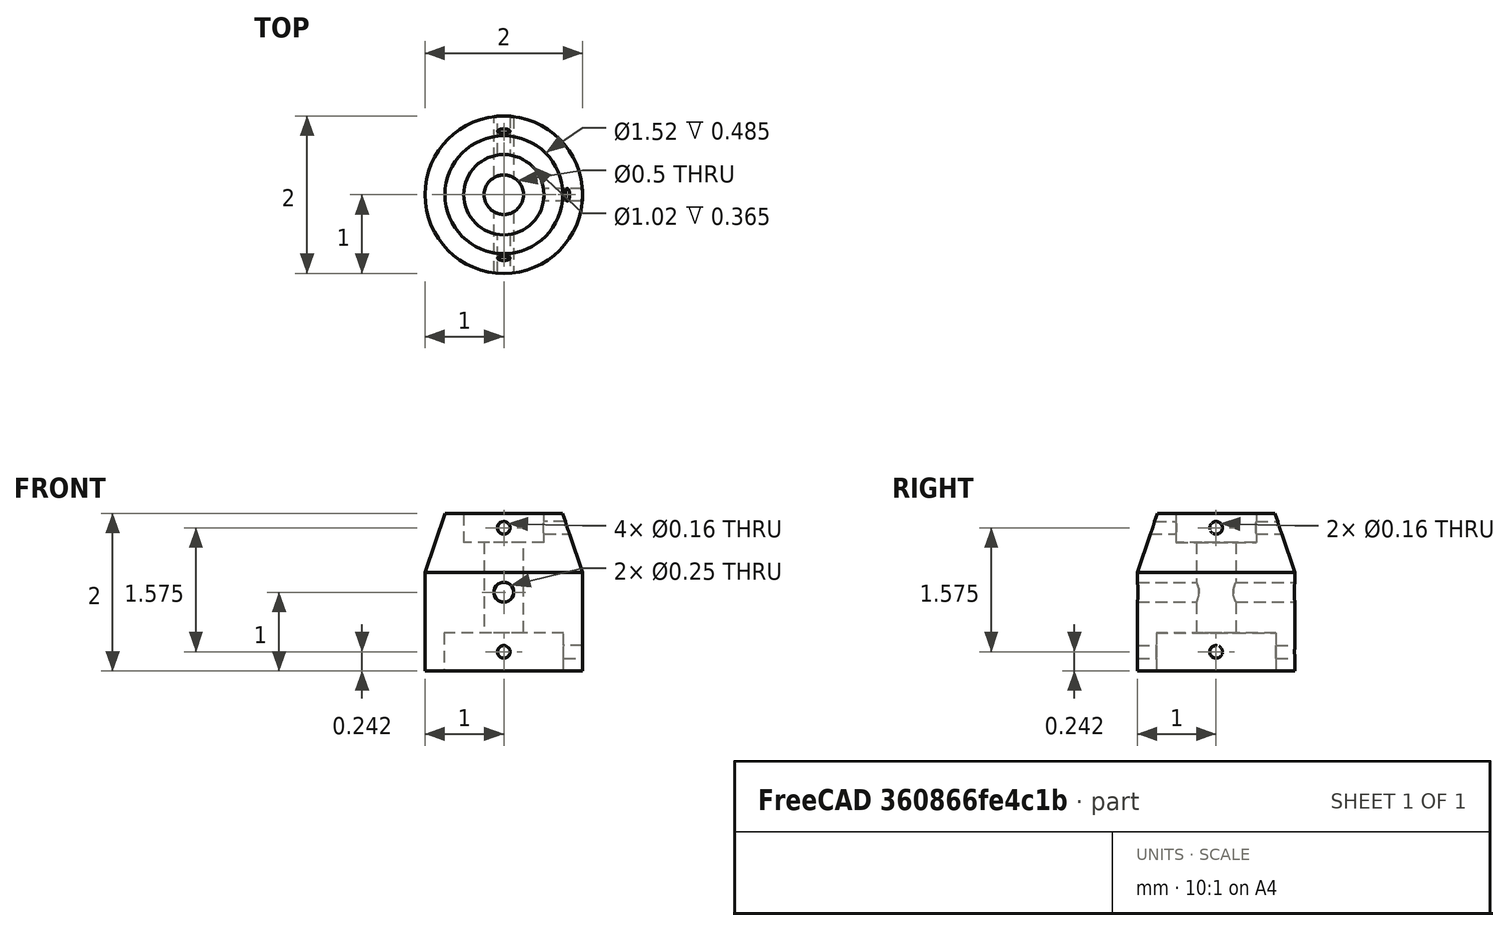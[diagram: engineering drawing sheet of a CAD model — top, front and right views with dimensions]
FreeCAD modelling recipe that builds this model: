
FCSTD DOCUMENT  (FreeCAD 0.20R29410 (Git))
Label: round_dies
License: All rights reserved
LicenseURL: http://en.wikipedia.org/wiki/All_rights_reserved
objects: Part::Cylinder×9, TechDraw::DrawViewDimension×9, TechDraw::DrawViewBalloon×7, TechDraw::DrawViewDimExtent×6, TechDraw::DrawProjGroupItem×2, TechDraw::DrawViewSection×2, Part::Cone×1, Part::Fuse×1, Part::MultiFuse×1, Part::Cut×1, TechDraw::DrawSVGTemplate×1, TechDraw::DrawProjGroup×1, TechDraw::DrawViewPart×1, TechDraw::DrawViewAnnotation×1, TechDraw::DrawPage×1
note: 13 computed .brp shape members not serialized (recipe doc carries the construction recipe); baked Part::Feature solids carry a one-line shape summary decoded from their .brp

FEATURE [Part::Cylinder] cylinder
  Angle = 360
  AttacherType = Attacher::AttachEngine3D
  FirstAngle = 0
  Height = 1.25
  Radius = 1
  SecondAngle = 0
FEATURE [Part::Cone] cylinder001
  Angle = 360
  AttacherType = Attacher::AttachEngine3D
  Height = 0.75
  Placement = pos=(0,0,1.25) rot=(0,0,1;0rad)
  Radius1 = 1
  Radius2 = 0.749
FEATURE [Part::Fuse] union
  Base = -> cylinder
  Tool = -> cylinder001
FEATURE [Part::Cylinder] cylinder002
  Angle = 360
  AttacherType = Attacher::AttachEngine3D
  FirstAngle = 0
  Height = 2.2
  Placement = pos=(0,0,-0.1) rot=(0,0,1;0rad)
  Radius = 0.2505
  SecondAngle = 0
FEATURE [Part::Cylinder] cylinder003
  Angle = 360
  AttacherType = Attacher::AttachEngine3D
  FirstAngle = 0
  Height = 0.585
  Placement = pos=(0,0,-0.1) rot=(0,0,1;0rad)
  Radius = 0.761
  SecondAngle = 0
FEATURE [Part::Cylinder] cylinder004
  Angle = 360
  AttacherType = Attacher::AttachEngine3D
  FirstAngle = 0
  Height = 0.465
  Placement = pos=(0,0,1.635) rot=(0,0,1;0rad)
  Radius = 0.51
  SecondAngle = 0
FEATURE [Part::Cylinder] cylinder005
  Angle = 360
  AttacherType = Attacher::AttachEngine3D
  FirstAngle = 0
  Height = 2.2
  Placement = pos=(0,1.1,1) rot=(1,0,0;1.5708rad)
  Radius = 0.1255
  SecondAngle = 0
FEATURE [Part::Cylinder] cylinder006
  Angle = 360
  AttacherType = Attacher::AttachEngine3D
  FirstAngle = 0
  Height = 2.2
  Placement = pos=(0,1.1,0.2425) rot=(1,0,0;1.5708rad)
  Radius = 0.0805
  SecondAngle = 0
FEATURE [Part::Cylinder] cylinder007
  Angle = 360
  AttacherType = Attacher::AttachEngine3D
  FirstAngle = 0
  Height = 2.2
  Placement = pos=(0,0,0.2425) rot=(0,1,0;1.5708rad)
  Radius = 0.0805
  SecondAngle = 0
FEATURE [Part::Cylinder] cylinder008
  Angle = 360
  AttacherType = Attacher::AttachEngine3D
  FirstAngle = 0
  Height = 2.2
  Placement = pos=(0,1.1,1.8175) rot=(1,0,0;1.5708rad)
  Radius = 0.0805
  SecondAngle = 0
FEATURE [Part::Cylinder] cylinder009
  Angle = 360
  AttacherType = Attacher::AttachEngine3D
  FirstAngle = 0
  Height = 2.2
  Placement = pos=(0,0,1.8175) rot=(0,1,0;1.5708rad)
  Radius = 0.0805
  SecondAngle = 0
FEATURE [Part::MultiFuse] union001
  Shapes = -> [cylinder002,cylinder003,cylinder004,cylinder005,cylinder006,cylinder007,cylinder008,cylinder009]
FEATURE [Part::Cut] difference
  Base = -> union
  Tool = -> union001
FEATURE [TechDraw::DrawSVGTemplate] Template001
  EditableTexts = Code=2022-10-20; CompanyAddress=<email> / Decatur, GA, US; CompanyName=Jason Antman; DrawingNumber=Rev. 1; DrawingTitle1=Round Tailstock Die Holder; DrawingTitle2=github.com/<owner>/machining-projects; DrawingTitle3=Based on design by Quinn Dunki; DrawnBy=<owner>; Sheet=Sheet 1 of 1
  Height = 215.9
  Orientation = 1
  Width = 279.4
FEATURE [TechDraw::DrawProjGroupItem] ProjItem  label="Front"
  CoarseView = false
  Direction = (0,0.707,0.707)
  Focus = 100
  HardHidden = false
  IsoCount = 0
  IsoHidden = false
  IsoVisible = true
  LockPosition = true
  Perspective = false
  Rotation = 0
  RotationVector = (1,0,0)
  ScaleType = 2
  SeamHidden = false
  SeamVisible = true
  SmoothHidden = false
  SmoothVisible = true
  Source = -> [difference]
  Type = 0
  X = 0
  XDirection = (1,0,0)
  Y = 0
FEATURE [TechDraw::DrawProjGroupItem] ProjItem001  label="Rear"
  CoarseView = false
  Direction = (0,-0.707107,-0.707107)
  Focus = 100
  HardHidden = false
  IsoCount = 0
  IsoHidden = false
  IsoVisible = true
  LockPosition = false
  Perspective = false
  Rotation = 0
  RotationVector = (1,0,0)
  ScaleType = 2
  SeamHidden = false
  SeamVisible = true
  SmoothHidden = false
  SmoothVisible = true
  Source = -> [difference]
  Type = 3
  X = 65
  XDirection = (-1,0,0)
  Y = 0
FEATURE [TechDraw::DrawProjGroup] ProjGroup
  Anchor = -> ProjItem
  AutoDistribute = true
  LockPosition = false
  ProjectionType = 0
  Rotation = 0
  Scale = 25
  ScaleType = 0
  Source = -> [difference]
  Views = -> [ProjItem,ProjItem001]
  X = 145.882
  Y = 154.566
  spacingX = 15
  spacingY = 15
FEATURE [TechDraw::DrawViewPart] View003  label="Top"
  CoarseView = false
  Direction = (0,-1,0)
  Focus = 100
  HardHidden = false
  IsoCount = 0
  IsoHidden = false
  IsoVisible = true
  LockPosition = false
  Perspective = false
  Rotation = 0
  Scale = 25
  ScaleType = 0
  SeamHidden = false
  SeamVisible = true
  SmoothHidden = false
  SmoothVisible = true
  Source = -> [difference]
  X = 70.6718
  XDirection = (1,0,0)
  Y = 59.6872
FEATURE [TechDraw::DrawViewDimension] Dimension010
  AngleOverride = false
  Arbitrary = false
  ArbitraryTolerances = false
  EqualTolerance = true
  ExtensionAngle = 0
  FormatSpec = %.3f
  FormatSpecOverTolerance = %+.3f
  FormatSpecUnderTolerance = %+.3f
  Inverted = false
  LineAngle = 0
  LockPosition = false
  MeasureType = 1
  OverTolerance = 0
  References2D = -> [View003]
  Rotation = 0
  Scale = 25
  ScaleType = 0
  TheoreticalExact = false
  Type = 2
  UnderTolerance = 0
  X = -42.5857
  Y = -3.32716
FEATURE [TechDraw::DrawViewDimension] Dimension011
  AngleOverride = false
  Arbitrary = false
  ArbitraryTolerances = false
  EqualTolerance = true
  ExtensionAngle = 0
  FormatSpec = %.3f
  FormatSpecOverTolerance = %+.3f
  FormatSpecUnderTolerance = %+.3f
  Inverted = false
  LineAngle = 0
  LockPosition = false
  MeasureType = 1
  OverTolerance = 0
  References2D = -> [View003]
  Rotation = 0
  Scale = 25
  ScaleType = 0
  TheoreticalExact = false
  Type = 2
  UnderTolerance = 0
  X = -42.6089
  Y = 18.6486
FEATURE [TechDraw::DrawViewBalloon] Balloon
  BubbleShape = 0
  EndType = 0
  EndTypeScale = 1
  KinkLength = 5
  LockPosition = false
  OriginX = 0.0752901
  OriginY = -0.785989
  Rotation = 0
  Scale = 25
  ScaleType = 0
  ShapeScale = 1
  SourceView = -> View003
  Text = 1
  TextWrapLen = -1
  X = 0.591536
  Y = -0.781057
FEATURE [TechDraw::DrawViewBalloon] Balloon001
  BubbleShape = 0
  EndType = 0
  EndTypeScale = 1
  KinkLength = 5
  LockPosition = false
  OriginX = 0.113048
  OriginY = -0.0545023
  Rotation = 0
  Scale = 25
  ScaleType = 0
  ShapeScale = 1
  SourceView = -> View003
  Text = 2
  TextWrapLen = -1
  X = 0.640981
  Y = -0.265215
FEATURE [TechDraw::DrawViewAnnotation] Annotation
  Font = osifont
  LineSpace = 80
  LockPosition = false
  MaxWidth = -1
  Rotation = 0
  ScaleType = 1
  Text = (1) Drill #20 & tap 10-24 at 0°, 90°, 180° | (2) Through-drill 1/4" and fit to rod | (3) Through-drill 1/2" and fit to rod
  TextSize = 5
  TextStyle = 0
  X = 206.899
  Y = 77.4786
FEATURE [TechDraw::DrawViewSection] SectionView  label="Section A"
  BaseView = -> View003
  CoarseView = false
  CutSurfaceDisplay = 2
  Direction = (1,0,0)
  FileGeomPattern = <path>
  FileHatchPattern = <path>
  Focus = 100
  FuseBeforeCut = false
  HardHidden = false
  HatchScale = 1
  IsoCount = 0
  IsoHidden = false
  IsoVisible = true
  LockPosition = false
  NameGeomPattern = Diamond
  Perspective = false
  Rotation = 0
  Scale = 25
  ScaleType = 0
  SeamHidden = false
  SeamVisible = true
  SectionDirection = 1
  SectionNormal = (1,0,0)
  SectionOrigin = (0,0,1)
  SmoothHidden = false
  SmoothVisible = true
  Source = -> [difference]
  X = 65.7076
  XDirection = (0,1,0)
  Y = 161.763
FEATURE [TechDraw::DrawViewDimension] Dimension
  AngleOverride = false
  Arbitrary = false
  ArbitraryTolerances = false
  EqualTolerance = true
  ExtensionAngle = 0
  FormatSpec = %.3f
  FormatSpecOverTolerance = %+.3f
  FormatSpecUnderTolerance = %+.3f
  Inverted = false
  LineAngle = 0
  LockPosition = false
  MeasureType = 1
  OverTolerance = 0
  References2D = -> [SectionView]
  Rotation = 0
  Scale = 25
  ScaleType = 0
  TheoreticalExact = false
  Type = 1
  UnderTolerance = 0
  X = 5.12673
  Y = 23.8695
FEATURE [TechDraw::DrawViewDimExtent] DimExtent002
  AngleOverride = false
  Arbitrary = false
  ArbitraryTolerances = false
  CosmeticTags = b452c0bf-c4f5-403c-97ec-773489345421 | 4a529553-57f1-47e3-98bc-15605a5df543
  DirExtent = 1
  EqualTolerance = true
  ExtensionAngle = 0
  FormatSpec = %.3f
  FormatSpecOverTolerance = %+.3f
  FormatSpecUnderTolerance = %+.3f
  Inverted = false
  LineAngle = 0
  LockPosition = false
  MeasureType = 1
  OverTolerance = 0
  References2D = -> [SectionView]
  Rotation = 0
  Scale = 25
  ScaleType = 0
  Source = -> [SectionView]
  TheoreticalExact = false
  Type = 2
  UnderTolerance = 0
  X = 31.9704
  Y = 11.0244
FEATURE [TechDraw::DrawViewDimExtent] DimExtent003
  AngleOverride = false
  Arbitrary = false
  ArbitraryTolerances = false
  CosmeticTags = 0415368b-dafb-4878-b81b-61ffdf83671d | 7fae5f09-d833-4bb3-b640-0a07f1f91ea6
  DirExtent = 1
  EqualTolerance = true
  ExtensionAngle = 0
  FormatSpec = %.3f
  FormatSpecOverTolerance = %+.3f
  FormatSpecUnderTolerance = %+.3f
  Inverted = false
  LineAngle = 0
  LockPosition = false
  MeasureType = 1
  OverTolerance = 0
  References2D = -> [SectionView]
  Rotation = 0
  Scale = 25
  ScaleType = 0
  Source = -> [SectionView]
  TheoreticalExact = false
  Type = 2
  UnderTolerance = 0
  X = 32.2769
  Y = -30.9794
FEATURE [TechDraw::DrawViewDimension] Dimension019
  AngleOverride = false
  Arbitrary = false
  ArbitraryTolerances = false
  EqualTolerance = true
  ExtensionAngle = 0
  FormatSpec = %.3f
  FormatSpecOverTolerance = %+.3f
  FormatSpecUnderTolerance = %+.3f
  Inverted = false
  LineAngle = 0
  LockPosition = false
  MeasureType = 1
  OverTolerance = 0
  References2D = -> [SectionView]
  Rotation = 0
  Scale = 25
  ScaleType = 0
  TheoreticalExact = false
  Type = 1
  UnderTolerance = 0
  X = 7.0309
  Y = -16.1319
FEATURE [TechDraw::DrawViewDimExtent] DimExtent004
  AngleOverride = false
  Arbitrary = false
  ArbitraryTolerances = false
  CosmeticTags = 438e6187-8641-4d19-a772-02b22118bba5 | e567fe35-3211-4887-a575-c20827386e03
  DirExtent = 0
  EqualTolerance = true
  ExtensionAngle = 0
  FormatSpec = %.3f
  FormatSpecOverTolerance = %+.3f
  FormatSpecUnderTolerance = %+.3f
  Inverted = false
  LineAngle = 0
  LockPosition = false
  MeasureType = 1
  OverTolerance = 0
  References2D = -> [SectionView]
  Rotation = 0
  Scale = 25
  ScaleType = 0
  Source = -> [SectionView]
  TheoreticalExact = false
  Type = 1
  UnderTolerance = 0
  X = 0
  Y = 0
FEATURE [TechDraw::DrawViewDimExtent] DimExtent005
  AngleOverride = false
  Arbitrary = false
  ArbitraryTolerances = false
  CosmeticTags = b63cf672-bbce-4496-b733-c79360275d39 | d015f4ed-4d79-42a1-81cd-ed7ba029a413
  DirExtent = 0
  EqualTolerance = true
  ExtensionAngle = 0
  FormatSpec = %.3f
  FormatSpecOverTolerance = %+.3f
  FormatSpecUnderTolerance = %+.3f
  Inverted = false
  LineAngle = 0
  LockPosition = false
  MeasureType = 1
  OverTolerance = 0
  References2D = -> [SectionView]
  Rotation = 0
  Scale = 25
  ScaleType = 0
  Source = -> [SectionView]
  TheoreticalExact = false
  Type = 1
  UnderTolerance = 0
  X = 11.4889
  Y = -26.492
FEATURE [TechDraw::DrawViewDimExtent] DimExtent006
  AngleOverride = false
  Arbitrary = false
  ArbitraryTolerances = false
  CosmeticTags = c31c85d9-741c-447f-8256-bb497a3bd161 | ec4dd3ef-5782-442c-9b18-a2a20b58f3c5
  DirExtent = 0
  EqualTolerance = true
  ExtensionAngle = 0
  FormatSpec = %.3f
  FormatSpecOverTolerance = %+.3f
  FormatSpecUnderTolerance = %+.3f
  Inverted = false
  LineAngle = 0
  LockPosition = false
  MeasureType = 1
  OverTolerance = 0
  References2D = -> [SectionView]
  Rotation = 0
  Scale = 25
  ScaleType = 0
  Source = -> [SectionView]
  TheoreticalExact = false
  Type = 1
  UnderTolerance = 0
  X = -0.540653
  Y = 36.8995
FEATURE [TechDraw::DrawViewBalloon] Balloon004
  BubbleShape = 0
  EndType = 0
  EndTypeScale = 1
  KinkLength = 5
  LockPosition = false
  OriginX = -0.0297067
  OriginY = 0.742682
  Rotation = 0
  Scale = 25
  ScaleType = 0
  ShapeScale = 1
  SourceView = -> View003
  Text = 1
  TextWrapLen = -1
  X = -0.554533
  Y = 0.508344
FEATURE [TechDraw::DrawViewDimension] Dimension021
  AngleOverride = false
  Arbitrary = false
  ArbitraryTolerances = false
  EqualTolerance = true
  ExtensionAngle = 0
  FormatSpec = %.3f
  FormatSpecOverTolerance = %+.3f
  FormatSpecUnderTolerance = %+.3f
  Inverted = false
  LineAngle = 0
  LockPosition = false
  MeasureType = 1
  OverTolerance = 0
  References2D = -> [SectionView]
  Rotation = 0
  Scale = 25
  ScaleType = 0
  TheoreticalExact = false
  Type = 6
  UnderTolerance = 0
  X = -35.735
  Y = 13.7801
FEATURE [TechDraw::DrawViewSection] SectionView001  label="Section B"
  BaseView = -> ProjItem
  CoarseView = false
  CutSurfaceDisplay = 1
  Direction = (-1,0,0)
  FileGeomPattern = <path>
  FileHatchPattern = <path>
  Focus = 100
  FuseBeforeCut = false
  HardHidden = false
  HatchScale = 1
  IsoCount = 0
  IsoHidden = false
  IsoVisible = true
  LockPosition = false
  NameGeomPattern = Diamond
  Perspective = false
  Rotation = 0
  Scale = 25
  ScaleType = 2
  SeamHidden = false
  SeamVisible = true
  SectionDirection = 0
  SectionNormal = (-1,0,0)
  SectionOrigin = (0,0,0.875)
  SmoothHidden = false
  SmoothVisible = true
  Source = -> [difference]
  X = 66.8864
  XDirection = (0,0.707107,0.707107)
  Y = 66.3839
FEATURE [TechDraw::DrawViewDimension] Dimension026
  AngleOverride = false
  Arbitrary = false
  ArbitraryTolerances = false
  EqualTolerance = true
  ExtensionAngle = 0
  FormatSpec = %.3f
  FormatSpecOverTolerance = %+.3f
  FormatSpecUnderTolerance = %+.3f
  Inverted = false
  LineAngle = 0
  LockPosition = false
  MeasureType = 1
  OverTolerance = 0
  References2D = -> [SectionView001]
  Rotation = 0
  Scale = 25
  ScaleType = 0
  TheoreticalExact = false
  Type = 0
  UnderTolerance = 0
  X = 22.1611
  Y = 42.226
FEATURE [TechDraw::DrawViewDimension] Dimension027
  AngleOverride = false
  Arbitrary = false
  ArbitraryTolerances = false
  EqualTolerance = true
  ExtensionAngle = 0
  FormatSpec = %.3f
  FormatSpecOverTolerance = %+.3f
  FormatSpecUnderTolerance = %+.3f
  Inverted = false
  LineAngle = 0
  LockPosition = false
  MeasureType = 1
  OverTolerance = 0
  References2D = -> [SectionView001]
  Rotation = 0
  Scale = 25
  ScaleType = 0
  TheoreticalExact = false
  Type = 0
  UnderTolerance = 0
  X = 14.1442
  Y = 38.5188
FEATURE [TechDraw::DrawViewDimension] Dimension028
  AngleOverride = false
  Arbitrary = false
  ArbitraryTolerances = false
  EqualTolerance = true
  ExtensionAngle = 0
  FormatSpec = %.3f
  FormatSpecOverTolerance = %+.3f
  FormatSpecUnderTolerance = %+.3f
  Inverted = false
  LineAngle = 0
  LockPosition = false
  MeasureType = 1
  OverTolerance = 0
  References2D = -> [SectionView001]
  Rotation = 0
  Scale = 25
  ScaleType = 0
  TheoreticalExact = false
  Type = 0
  UnderTolerance = 0
  X = 34.4996
  Y = 9.08217
FEATURE [TechDraw::DrawViewDimension] Dimension029
  AngleOverride = false
  Arbitrary = false
  ArbitraryTolerances = false
  EqualTolerance = true
  ExtensionAngle = 0
  FormatSpec = %.3f
  FormatSpecOverTolerance = %+.3f
  FormatSpecUnderTolerance = %+.3f
  Inverted = false
  LineAngle = 0
  LockPosition = false
  MeasureType = 1
  OverTolerance = 0
  References2D = -> [SectionView]
  Rotation = 0
  Scale = 25
  ScaleType = 0
  TheoreticalExact = false
  Type = 0
  UnderTolerance = 0
  X = 48.9147
  Y = 4.74177
FEATURE [TechDraw::DrawViewBalloon] Balloon005
  BubbleShape = 0
  EndType = 0
  EndTypeScale = 1
  KinkLength = 5
  LockPosition = false
  OriginX = 5.58735e-10
  OriginY = 0.452548
  Rotation = 0
  Scale = 25
  ScaleType = 0
  ShapeScale = 1
  SourceView = -> ProjItem001
  Text = 3
  TextWrapLen = -1
  X = 1.44762
  Y = 0.816649
FEATURE [TechDraw::DrawViewBalloon] Balloon006
  BubbleShape = 0
  EndType = 0
  EndTypeScale = 1
  KinkLength = 5
  LockPosition = false
  OriginX = 0
  OriginY = -0.707107
  Rotation = 0
  Scale = 25
  ScaleType = 0
  ShapeScale = 1
  SourceView = -> ProjItem001
  Text = 2
  TextWrapLen = -1
  X = 1.54726
  Y = -0.691726
FEATURE [TechDraw::DrawViewBalloon] Balloon007
  BubbleShape = 0
  EndType = 0
  EndTypeScale = 1
  KinkLength = 5
  LockPosition = false
  OriginX = 0
  OriginY = -0.203293
  Rotation = 0
  Scale = 25
  ScaleType = 0
  ShapeScale = 1
  SourceView = -> ProjItem001
  Text = 1
  TextWrapLen = -1
  X = 1.5348
  Y = 0.048719
FEATURE [TechDraw::DrawViewBalloon] Balloon008
  BubbleShape = 0
  EndType = 0
  EndTypeScale = 1
  KinkLength = 5
  LockPosition = false
  OriginX = 1.30159e-09
  OriginY = -1.20174
  Rotation = 0
  Scale = 25
  ScaleType = 0
  ShapeScale = 1
  SourceView = -> ProjItem001
  Text = 1
  TextWrapLen = -1
  X = 1.52235
  Y = -1.24863
FEATURE [TechDraw::DrawViewDimExtent] DimExtent
  AngleOverride = false
  Arbitrary = false
  ArbitraryTolerances = false
  CosmeticTags = f97bde55-d9ef-41df-b53e-99bd78d8dca1 | d09bd855-3c48-4334-a38d-2d095375d641
  DirExtent = 1
  EqualTolerance = true
  ExtensionAngle = 0
  FormatSpec = %.3f
  FormatSpecOverTolerance = %+.3f
  FormatSpecUnderTolerance = %+.3f
  Inverted = false
  LineAngle = 0
  LockPosition = false
  MeasureType = 1
  OverTolerance = 0
  References2D = -> [SectionView]
  Rotation = 0
  Scale = 25
  ScaleType = 0
  Source = -> [SectionView]
  TheoreticalExact = false
  Type = 2
  UnderTolerance = 0
  X = -33.9502
  Y = -5.63193
FEATURE [TechDraw::DrawPage] Page001
  KeepUpdated = true
  NextBalloonIndex = 15
  ProjectionType = 0
  Scale = 25
  Template = -> Template001
  Views = -> [ProjGroup,View003,Dimension010,Dimension011,Balloon,Balloon001,Annotation,SectionView,Dimension,DimExtent002,DimExtent003,Dimension019,DimExtent004,DimExtent005,DimExtent006,Balloon004,Dimension021,SectionView001,Dimension026,Dimension027,Dimension028,Dimension029,Balloon005,Balloon006,Balloon007,Balloon008,DimExtent]
note: 4 file-system paths scrubbed to <path> (originals preserved in the JSON sidecar)
